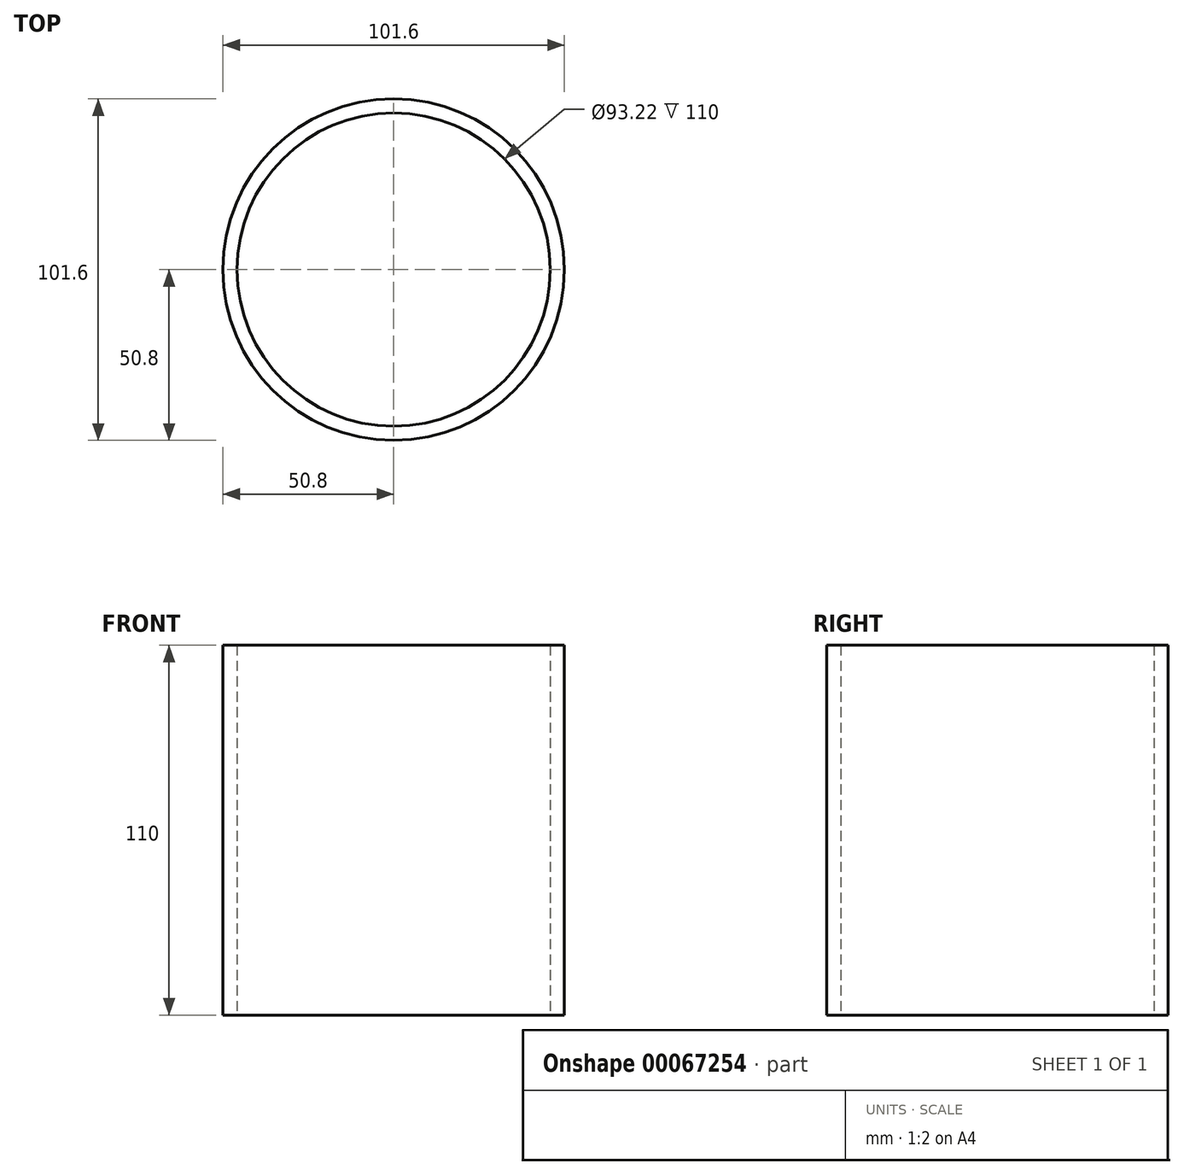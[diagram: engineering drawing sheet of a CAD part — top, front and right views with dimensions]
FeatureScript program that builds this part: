
annotation { "Feature Type Name" : "Feature", "Feature Type Description" : "" }
export const myFeature = defineFeature(function(context is Context, id is Id, definition is map)
    precondition{}
    {
        {
            var Q0;
            Q0=qCreatedBy(makeId("Top.planeOp"),FACE);
            var sketch = newSketch(context, id + "F0", { "sketchPlane" : qUnion([Q0])});
            skCircle(sketch, "E0", {"center": v(0, 0) * mm, "radius": 50.8 * mm});
            skCircle(sketch, "E1", {"center": v(0, 0) * mm, "radius": 46.6 * mm});
            skSolve(sketch);
        }
        {
            var Q0;
            Q0=makeQuery(id+"F0.imprint","IMPRINT",FACE,{"disambiguationData":[TD([[makeQuery(id+"F0.imprint","IMPRINT",EDGE,{"derivedFrom":sQuery(id+"F0.wireOp",EDGE,"E0")}),-1.0]])]});
            var Q1;
            Q1=makeQuery(id+"F0.imprint","IMPRINT",FACE,{"disambiguationData":[TD([[makeQuery(id+"F0.imprint","IMPRINT",EDGE,{"derivedFrom":sQuery(id+"F0.wireOp",EDGE,"E0")}),1.0]])]});
            extrude(context, id + "F1", {"entities" : qUnion([Q0, Q1]), "depth" : 110 * mm});
        }
    });
